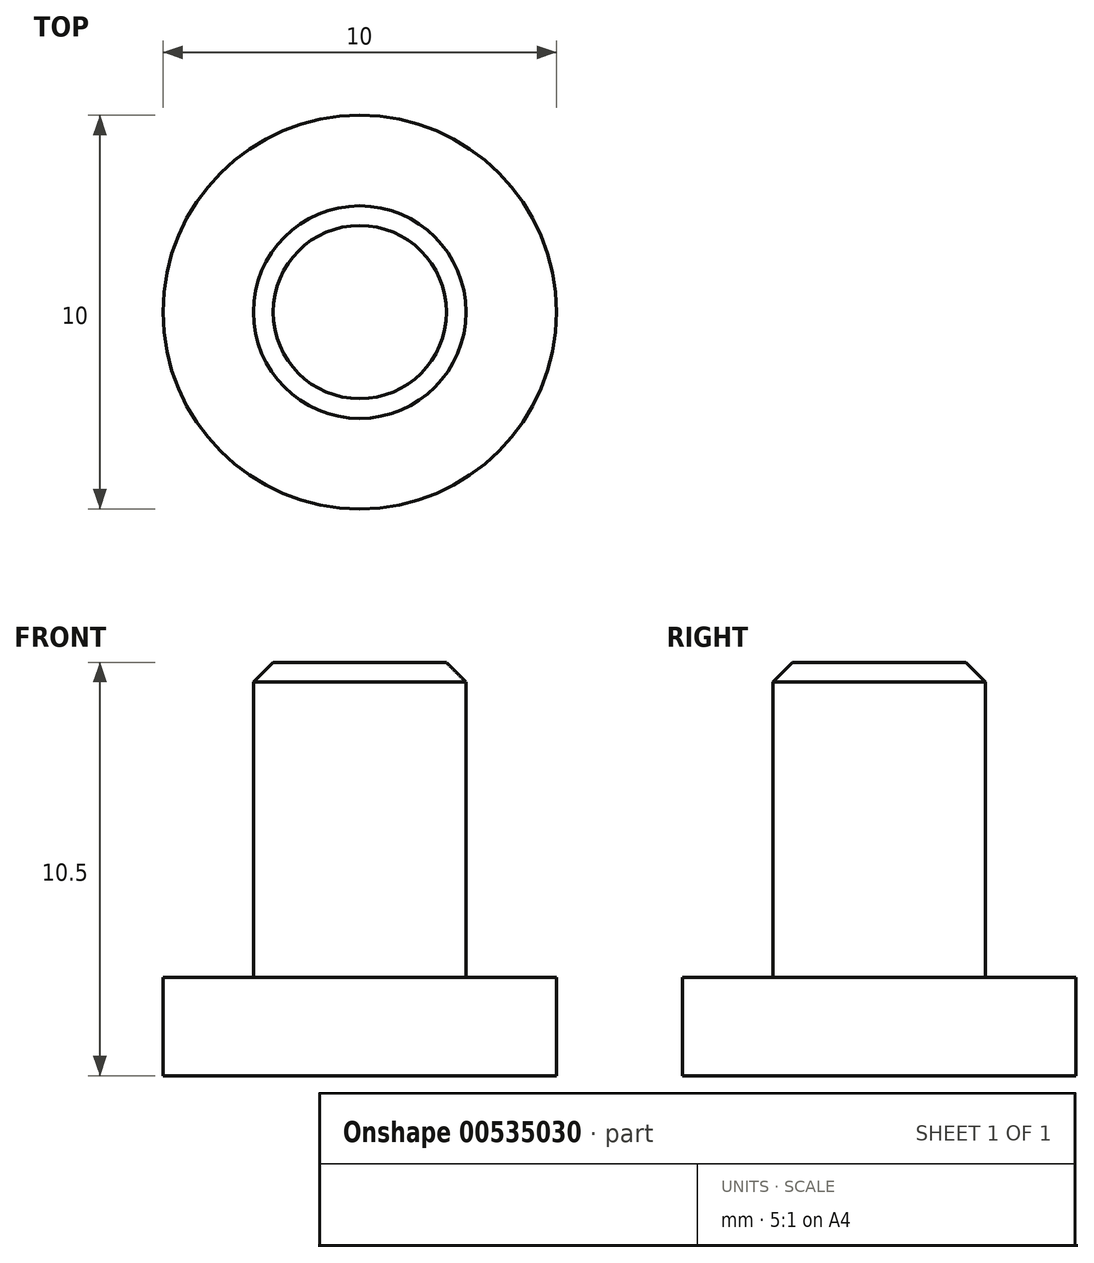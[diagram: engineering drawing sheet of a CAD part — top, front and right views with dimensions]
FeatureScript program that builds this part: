
annotation { "Feature Type Name" : "Feature", "Feature Type Description" : "" }
export const myFeature = defineFeature(function(context is Context, id is Id, definition is map)
    precondition{}
    {
        {
            var Q0;
            Q0=qCreatedBy(makeId("Top.planeOp"),FACE);
            var sketch = newSketch(context, id + "F0", { "sketchPlane" : qUnion([Q0])});
            skCircle(sketch, "E0", {"center": v(0, 0) * mm, "radius": 5 * mm});
            skSolve(sketch);
        }
        {
            var Q0;
            Q0=makeQuery(id+"F0.imprint","IMPRINT",FACE,{"disambiguationData":[TD([[makeQuery(id+"F0.imprint","IMPRINT",EDGE,{"derivedFrom":sQuery(id+"F0.wireOp",EDGE,"E0")}),1.0]])]});
            extrude(context, id + "F1", {"entities" : qUnion([Q0]), "depth" : 2.5 * mm, "offsetDistance" : 25 * mm});
        }
        {
            var Q0;
            Q0=makeQuery(id+"F1.opExtrude","CAP_FACE",FACE,{"disambiguationData":[OSD([sQuery(id+"F0.wireOp",EDGE,"E0")])],"isStart":false});
            var sketch = newSketch(context, id + "F2", { "sketchPlane" : qUnion([Q0])});
            skCircle(sketch, "E1", {"center": v(0, 0) * mm, "radius": 2.7 * mm});
            skSolve(sketch);
        }
        {
            var Q0;
            Q0 = qSketchRegion(id + "F2", true);
            extrude(context, id + "F3", {"entities" : qUnion([Q0]), "operationType" : NewBodyOperationType.ADD, "depth" : 8 * mm, "offsetDistance" : 25 * mm});
        }
        {
            var Q0;
            Q0=makeQuery(id+"F3.opExtrude","CAP_EDGE",EDGE,{"disambiguationData":[OSD([sQuery(id+"F2.wireOp",EDGE,"E1")])],"isStart":false});
            chamfer(context, id + "F4", {"entities" : qUnion([Q0]), "width" : .5 * mm, "tangentPropagation" : true});
        }
    });
